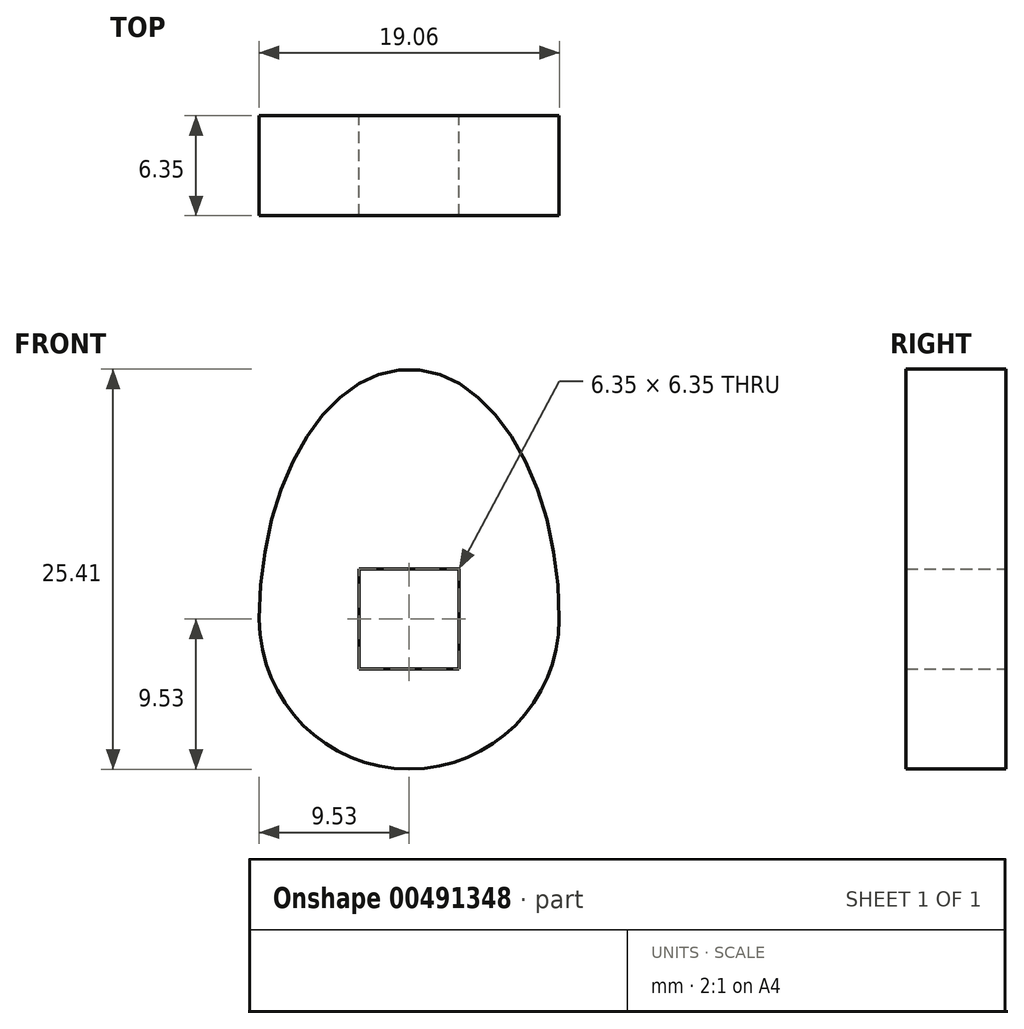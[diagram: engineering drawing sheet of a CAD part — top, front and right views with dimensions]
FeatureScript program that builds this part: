
annotation { "Feature Type Name" : "Feature", "Feature Type Description" : "" }
export const myFeature = defineFeature(function(context is Context, id is Id, definition is map)
    precondition{}
    {
        {
            var Q0;
            Q0=qCreatedBy(makeId("Front.planeOp"),FACE);
            var sketch = newSketch(context, id + "F0", { "sketchPlane" : qUnion([Q0])});
            skEllipse(sketch, "E0", {"center": v(0, 0) * mm, "majorRadius": 15.88 * mm, "minorRadius": 9.53 * mm, "majorAxis": v(0, -1)});
            skCircle(sketch, "E1", {"center": v(0, 0) * mm, "radius": 9.53 * mm});
            skPoint(sketch, "E2", {"position": v(0, -9.53) * mm});
            skPoint(sketch, "E3", {"position": v(0, 15.88) * mm});
            skLineSegment(sketch, "E4.bottom", {"start": v(3.18, 3.18) * mm, "end": v(-3.18, 3.18) * mm});
            skLineSegment(sketch, "E4.top", {"start": v(3.18, -3.18) * mm, "end": v(-3.18, -3.18) * mm});
            skLineSegment(sketch, "E4.left", {"start": v(3.18, 3.18) * mm, "end": v(3.18, -3.18) * mm});
            skLineSegment(sketch, "E4.right", {"start": v(-3.18, 3.18) * mm, "end": v(-3.18, -3.18) * mm});
            skSolve(sketch);
        }
        {
            var Q0;
            {var subQ0=sQuery(id+"F0.wireOp",EDGE,"E1");var subQ1=sQuery(id+"F0.wireOp",EDGE,"E0");var subQ2=makeQuery(id+"F0.imprint","INTERSECT",VERTEX,{"disambiguationData":[OD(0.0)],"derivedFrom":[subQ1,subQ0]});Q0=makeQuery(id+"F0.imprint","IMPRINT",FACE,{"disambiguationData":[TD([[makeQuery(id+"F0.imprint","IMPRINT",EDGE,{"disambiguationData":[TD([[subQ2,1.0]])],"derivedFrom":subQ1}),1.0]])]});}
            var Q1;
            Q1=makeQuery(id+"F0.imprint","IMPRINT",FACE,{"disambiguationData":[TD([[makeQuery(id+"F0.imprint","IMPRINT",EDGE,{"derivedFrom":sQuery(id+"F0.wireOp",EDGE,"E4.bottom")}),-1.0]])]});
            extrude(context, id + "F1", {"entities" : qUnion([Q0, Q1]), "depth" : 6.35 * mm});
        }
    });
